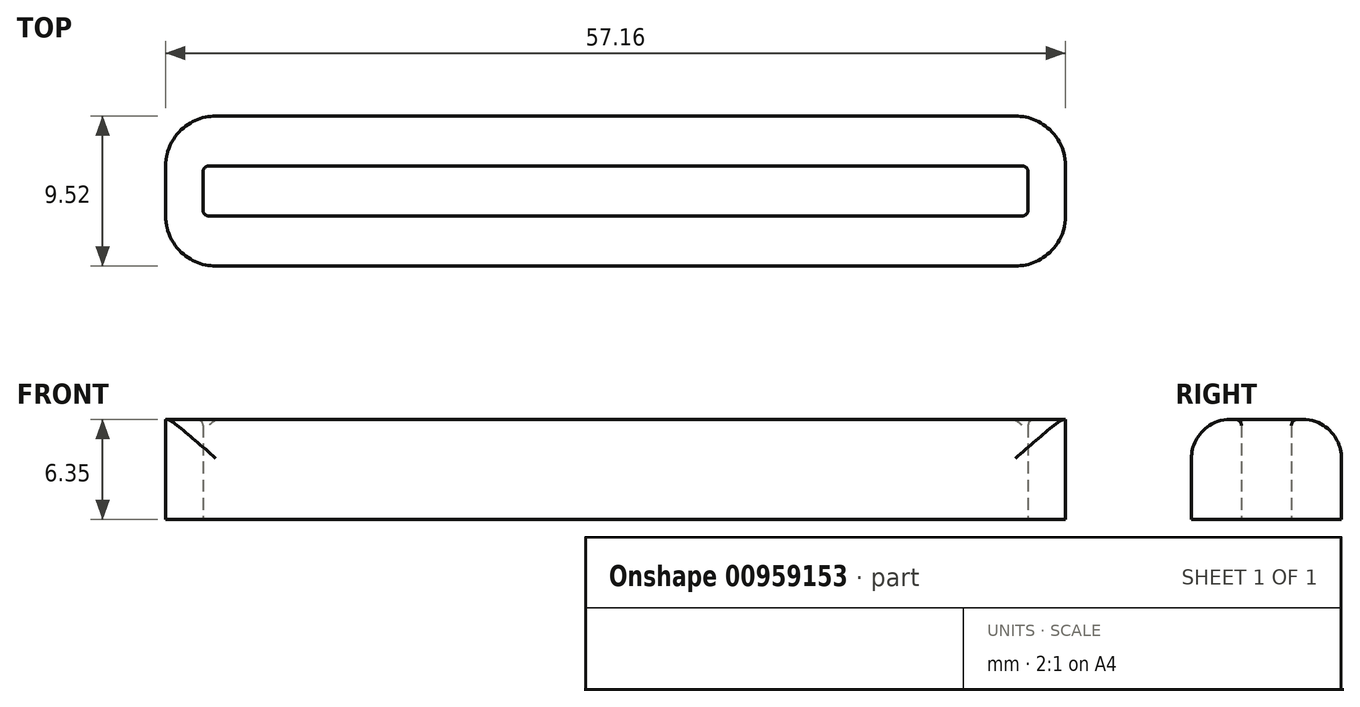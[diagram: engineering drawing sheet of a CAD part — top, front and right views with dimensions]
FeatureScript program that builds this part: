
annotation { "Feature Type Name" : "Feature", "Feature Type Description" : "" }
export const myFeature = defineFeature(function(context is Context, id is Id, definition is map)
    precondition{}
    {
        {
            var Q0;
            Q0=qCreatedBy(makeId("Top.planeOp"),FACE);
            var sketch = newSketch(context, id + "F0", { "sketchPlane" : qUnion([Q0])});
            skLineSegment(sketch, "E0.bottom", {"start": v(-25.4, 4.76) * mm, "end": v(25.4, 4.76) * mm});
            skLineSegment(sketch, "E0.top", {"start": v(-25.4, -4.76) * mm, "end": v(25.4, -4.76) * mm});
            skLineSegment(sketch, "E0.left", {"start": v(-28.58, 1.59) * mm, "end": v(-28.58, -1.59) * mm});
            skLineSegment(sketch, "E0.right", {"start": v(28.58, 1.59) * mm, "end": v(28.58, -1.59) * mm});
            skPoint(sketch, "E0.middle", {"position": v(0, 0) * mm});
            skPoint(sketch, "E1.visualSharp", {"position": v(-28.57, 4.76) * mm});
            skArc(sketch, "E1.filletArc", {"start": v(-25.4, 4.76) * mm, "mid": v(-27.65, 3.83) * mm, "end": v(-28.58, 1.59) * mm});
            skPoint(sketch, "E2.visualSharp", {"position": v(-28.58, -4.76) * mm});
            skArc(sketch, "E2.filletArc", {"start": v(-28.58, -1.59) * mm, "mid": v(-27.65, -3.83) * mm, "end": v(-25.4, -4.76) * mm});
            skPoint(sketch, "E3.visualSharp", {"position": v(28.57, -4.76) * mm});
            skArc(sketch, "E3.filletArc", {"start": v(25.4, -4.76) * mm, "mid": v(27.65, -3.83) * mm, "end": v(28.57, -1.59) * mm});
            skPoint(sketch, "E4.visualSharp", {"position": v(28.57, 4.76) * mm});
            skArc(sketch, "E4.filletArc", {"start": v(28.57, 1.59) * mm, "mid": v(27.65, 3.83) * mm, "end": v(25.4, 4.76) * mm});
            skLineSegment(sketch, "E5.bottom", {"start": v(26.2, -1.59) * mm, "end": v(-26.2, -1.59) * mm});
            skLineSegment(sketch, "E5.top", {"start": v(26.2, 1.59) * mm, "end": v(-26.2, 1.59) * mm});
            skLineSegment(sketch, "E5.left", {"start": v(26.2, -1.59) * mm, "end": v(26.2, 1.59) * mm});
            skLineSegment(sketch, "E5.right", {"start": v(-26.2, -1.59) * mm, "end": v(-26.2, 1.59) * mm});
            skSolve(sketch);
        }
        {
            var Q0;
            Q0=makeQuery(id+"F0.imprint","IMPRINT",FACE,{"disambiguationData":[TD([[makeQuery(id+"F0.imprint","IMPRINT",EDGE,{"derivedFrom":sQuery(id+"F0.wireOp",EDGE,"E0.bottom")}),-1.0]])]});
            extrude(context, id + "F1", {"entities" : qUnion([Q0]), "depth" : 6.35 * mm, "offsetDistance" : 25.4 * mm});
        }
        {
            var Q0;
            Q0=makeQuery(id+"F1.opExtrude","CAP_EDGE",EDGE,{"disambiguationData":[OSD([sQuery(id+"F0.wireOp",EDGE,"E0.top")])],"isStart":false});
            var Q1;
            Q1=makeQuery(id+"F1.opExtrude","CAP_EDGE",EDGE,{"disambiguationData":[OSD([sQuery(id+"F0.wireOp",EDGE,"E0.bottom")])],"isStart":false});
            fillet(context, id + "F2", {"entities" : qUnion([Q0, Q1]), "radius" : 2.46 * mm, "allowEdgeOverflow" : false});
        }
        {
            var Q0;
            Q0=makeQuery(id+"F1.opExtrude","CAP_EDGE",EDGE,{"disambiguationData":[OSD([sQuery(id+"F0.wireOp",EDGE,"E5.right")])],"isStart":false});
            var Q1;
            Q1=makeQuery(id+"F1.opExtrude","CAP_EDGE",EDGE,{"disambiguationData":[OSD([sQuery(id+"F0.wireOp",EDGE,"E5.left")])],"isStart":false});
            var Q2;
            Q2=makeQuery(id+"F1.opExtrude","SWEPT_EDGE",EDGE,{"disambiguationData":[OSD([sQuery(id+"F0.wireOp",EDGE,"E5.top"),sQuery(id+"F0.wireOp",EDGE,"E5.right")])]});
            var Q3;
            Q3=makeQuery(id+"F1.opExtrude","SWEPT_EDGE",EDGE,{"disambiguationData":[OSD([sQuery(id+"F0.wireOp",EDGE,"E5.top"),sQuery(id+"F0.wireOp",EDGE,"E5.left")])]});
            var Q4;
            Q4=makeQuery(id+"F1.opExtrude","SWEPT_EDGE",EDGE,{"disambiguationData":[OSD([sQuery(id+"F0.wireOp",EDGE,"E5.bottom"),sQuery(id+"F0.wireOp",EDGE,"E5.left")])]});
            var Q5;
            Q5=makeQuery(id+"F1.opExtrude","SWEPT_EDGE",EDGE,{"disambiguationData":[OSD([sQuery(id+"F0.wireOp",EDGE,"E5.bottom"),sQuery(id+"F0.wireOp",EDGE,"E5.right")])]});
            fillet(context, id + "F3", {"entities" : qUnion([Q0, Q1, Q2, Q3, Q4, Q5]), "radius" : 0.38 * mm, "allowEdgeOverflow" : false});
        }
    });
